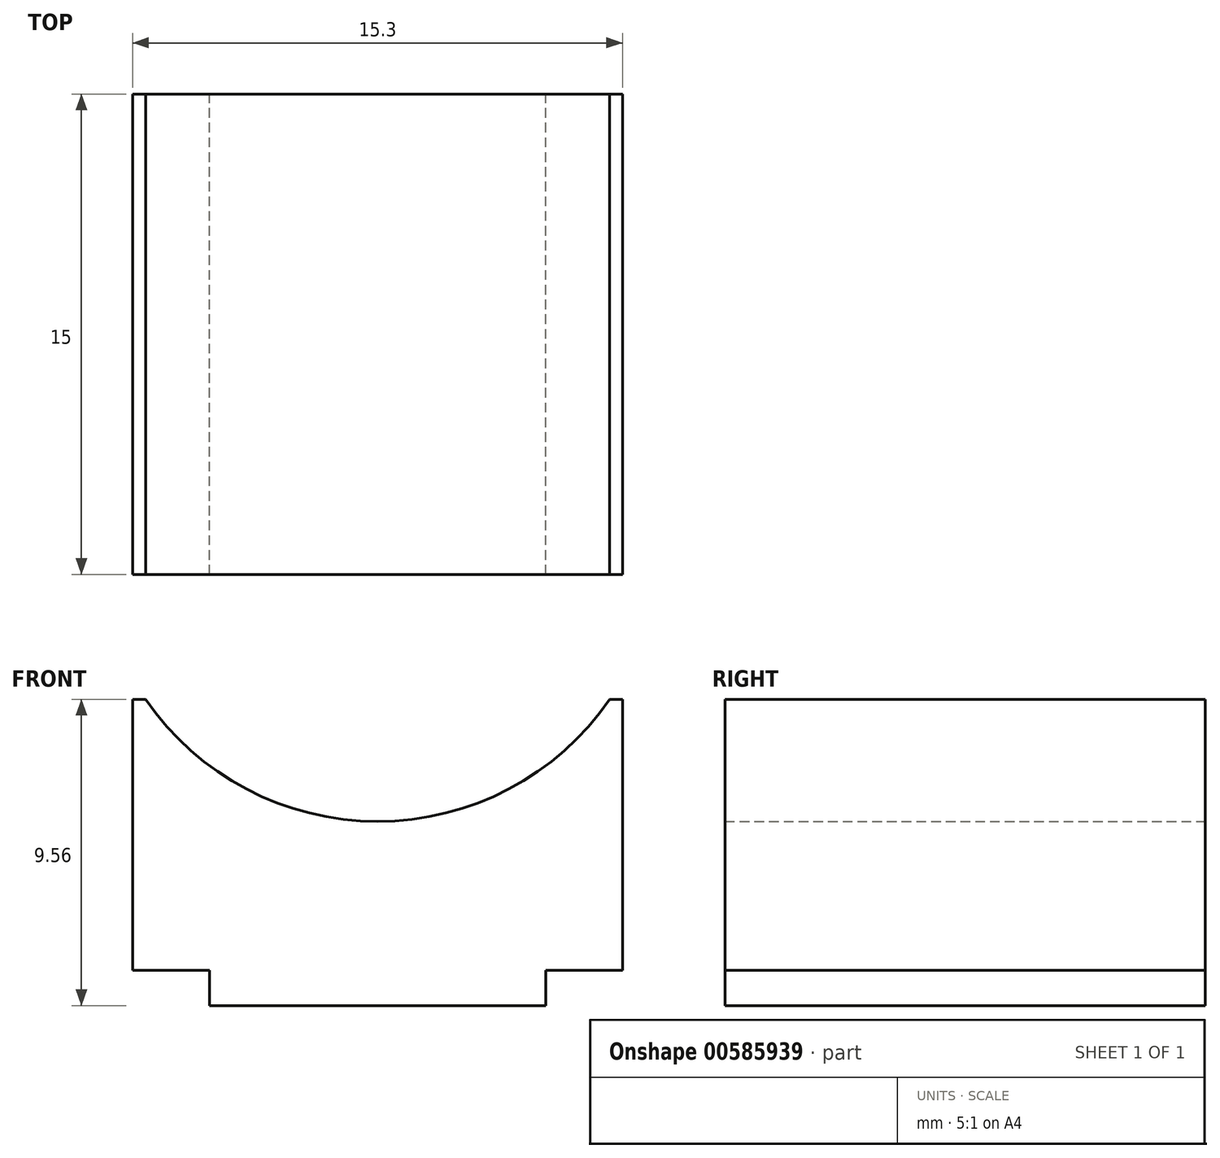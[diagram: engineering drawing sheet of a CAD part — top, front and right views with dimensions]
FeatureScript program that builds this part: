
annotation { "Feature Type Name" : "Feature", "Feature Type Description" : "" }
export const myFeature = defineFeature(function(context is Context, id is Id, definition is map)
    precondition{}
    {
        {
            var Q0;
            Q0=qCreatedBy(makeId("Front.planeOp"),FACE);
            var sketch = newSketch(context, id + "F0", { "sketchPlane" : qUnion([Q0])});
            skLineSegment(sketch, "E0", {"start": v(7.25, 4.78) * mm, "end": v(7.65, 4.78) * mm});
            skArc(sketch, "E1", {"start": v(0, 0.97) * mm, "mid": v(4.1, 1.98) * mm, "end": v(7.25, 4.78) * mm});
            skLineSegment(sketch, "E2", {"start": v(5.25, -3.68) * mm, "end": v(7.65, -3.68) * mm});
            skLineSegment(sketch, "E3", {"start": v(5.25, -3.68) * mm, "end": v(5.25, -4.78) * mm});
            skLineSegment(sketch, "E4", {"start": v(7.65, 4.78) * mm, "end": v(7.65, -3.68) * mm});
            skLineSegment(sketch, "E5", {"start": v(0, -4.78) * mm, "end": v(5.25, -4.78) * mm});
            skLineSegment(sketch, "E6", {"start": v(-7.25, 4.78) * mm, "end": v(-7.65, 4.78) * mm});
            skArc(sketch, "E7", {"start": v(-7.25, 4.78) * mm, "mid": v(-4.1, 1.98) * mm, "end": v(0, 0.97) * mm});
            skLineSegment(sketch, "E8", {"start": v(-5.25, -3.68) * mm, "end": v(-7.65, -3.68) * mm});
            skLineSegment(sketch, "E9", {"start": v(-5.25, -3.68) * mm, "end": v(-5.25, -4.78) * mm});
            skLineSegment(sketch, "E10", {"start": v(-7.65, 4.78) * mm, "end": v(-7.65, -3.68) * mm});
            skLineSegment(sketch, "E11", {"start": v(0, -4.78) * mm, "end": v(-5.25, -4.78) * mm});
            skSolve(sketch);
        }
        {
            var Q0;
            Q0=makeQuery(id+"F0.imprint","IMPRINT",FACE,{"disambiguationData":[TD([[makeQuery(id+"F0.imprint","IMPRINT",EDGE,{"derivedFrom":sQuery(id+"F0.wireOp",EDGE,"E0")}),-1.0]])]});
            extrude(context, id + "F1", {"entities" : qUnion([Q0]), "depth" : 15 * mm, "offsetDistance" : 25.4 * mm});
        }
    });
